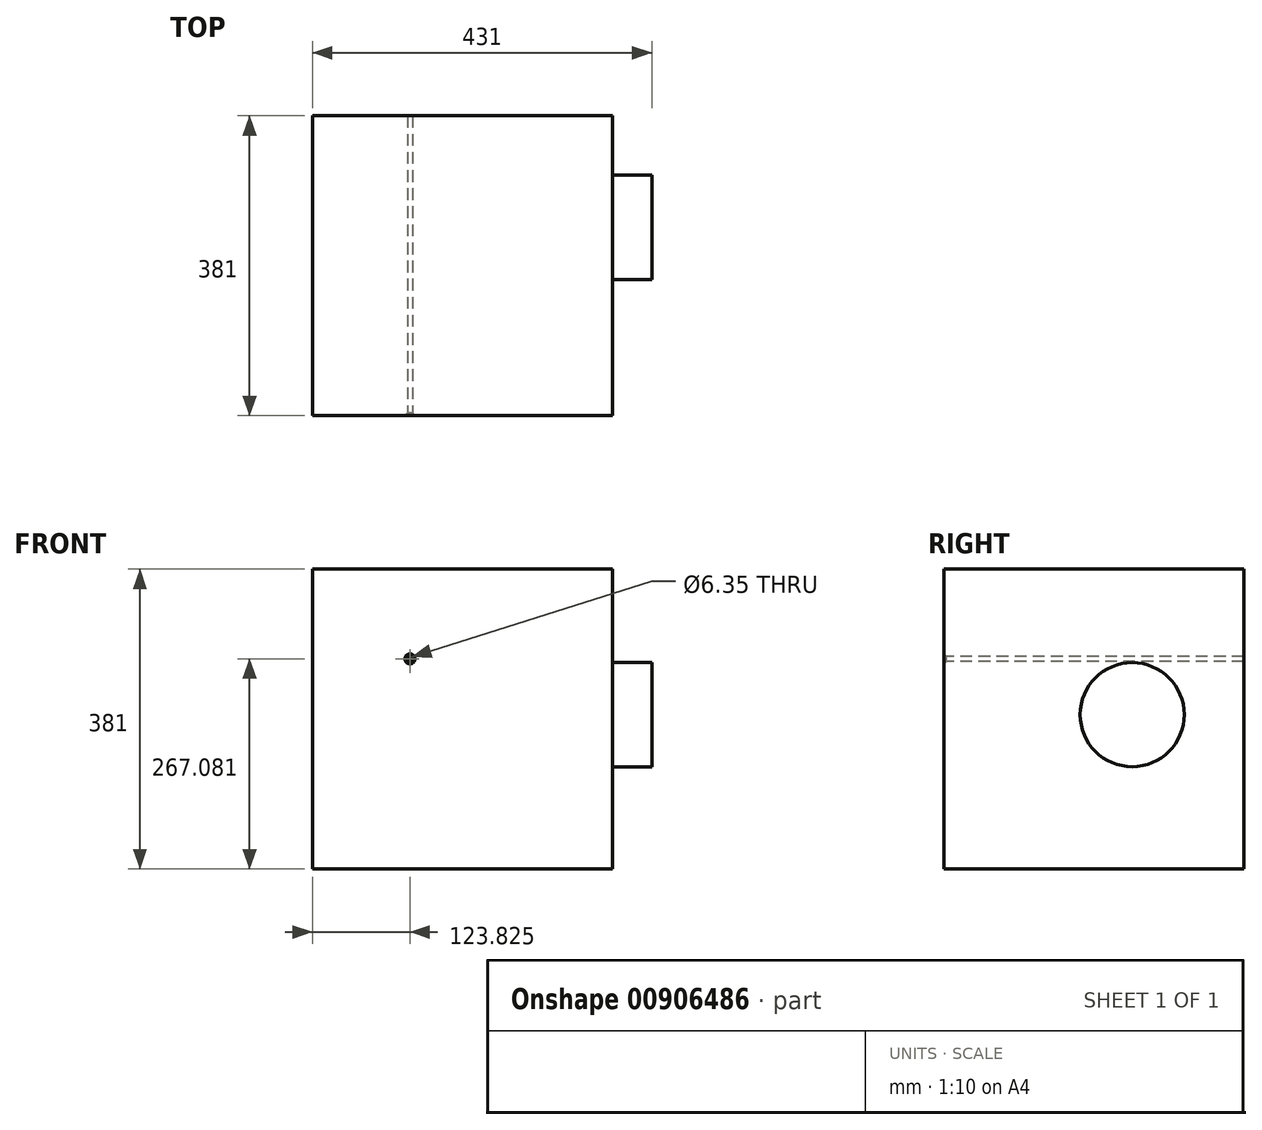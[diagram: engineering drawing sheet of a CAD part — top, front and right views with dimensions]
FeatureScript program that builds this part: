
annotation { "Feature Type Name" : "Feature", "Feature Type Description" : "" }
export const myFeature = defineFeature(function(context is Context, id is Id, definition is map)
    precondition{}
    {
        {
            var Q0;
            Q0=qCreatedBy(makeId("Front.planeOp"),FACE);
            var sketch = newSketch(context, id + "F0", { "sketchPlane" : qUnion([Q0])});
            skLineSegment(sketch, "E0.bottom", {"start": v(0, 0) * mm, "end": v(381, 0) * mm});
            skLineSegment(sketch, "E0.top", {"start": v(0, 381) * mm, "end": v(381, 381) * mm});
            skLineSegment(sketch, "E0.left", {"start": v(0, 0) * mm, "end": v(0, 381) * mm});
            skLineSegment(sketch, "E0.right", {"start": v(381, 0) * mm, "end": v(381, 381) * mm});
            skSolve(sketch);
        }
        {
            var Q0;
            Q0=qSketchRegion(id+"F0",true);
            extrude(context, id + "F1", {"entities" : qUnion([Q0]), "depth" : 381 * mm, "offsetDistance" : 25.4 * mm});
        }
        {
            var Q0;
            Q0=makeQuery(id+"F1.opExtrude","CAP_FACE",FACE,{"disambiguationData":[OSD([sQuery(id+"F0.wireOp",EDGE,"E0.bottom"),sQuery(id+"F0.wireOp",EDGE,"E0.top"),sQuery(id+"F0.wireOp",EDGE,"E0.left"),sQuery(id+"F0.wireOp",EDGE,"E0.right")])],"isStart":false});
            var sketch = newSketch(context, id + "F2", { "sketchPlane" : qUnion([Q0])});
            skPoint(sketch, "E1", {"position": v(123.83, 267.08) * mm});
            skSolve(sketch);
        }
        {
            var Q0;
            Q0=sQuery(id+"F2.wireOp",VERTEX,"E1");
            var Q1;
            Q1=makeQuery(id+"F1.opExtrude","SWEPT_BODY",BODY,{"disambiguationData":[OSD([sQuery(id+"F0.wireOp",EDGE,"E0.bottom"),sQuery(id+"F0.wireOp",EDGE,"E0.top"),sQuery(id+"F0.wireOp",EDGE,"E0.left"),sQuery(id+"F0.wireOp",EDGE,"E0.right")])]});
            hole(context, id + "F3", {"style" : HoleStyle.C_SINK, "endStyle" : HoleEndStyle.THROUGH, "holeDiameter" : 6.35 * mm, "cSinkDiameter" : 12.7 * mm, "cSinkAngle" : 90 * degree, "majorDiameter" : 6.35 * mm, "isTappedThrough" : true, "tappedDepth" : 12.7 * mm, "tapClearance" : 3, "locations" : qUnion([Q0]), "scope" : qUnion([Q1])});
        }
        {
            var Q0;
            Q0=makeQuery(id+"F1.opExtrude","SWEPT_FACE",FACE,{"disambiguationData":[OSD([sQuery(id+"F0.wireOp",EDGE,"E0.right")])]});
            var sketch = newSketch(context, id + "F4", { "sketchPlane" : qUnion([Q0])});
            skCircle(sketch, "E2", {"center": v(-141.75, 196.2) * mm, "radius": 66.12 * mm});
            skSolve(sketch);
        }
        {
            var Q0;
            Q0=qSketchRegion(id+"F4",true);
            extrude(context, id + "F5", {"entities" : qUnion([Q0]), "operationType" : NewBodyOperationType.ADD, "depth" : 50 * mm, "offsetDistance" : 25 * mm});
        }
    });
